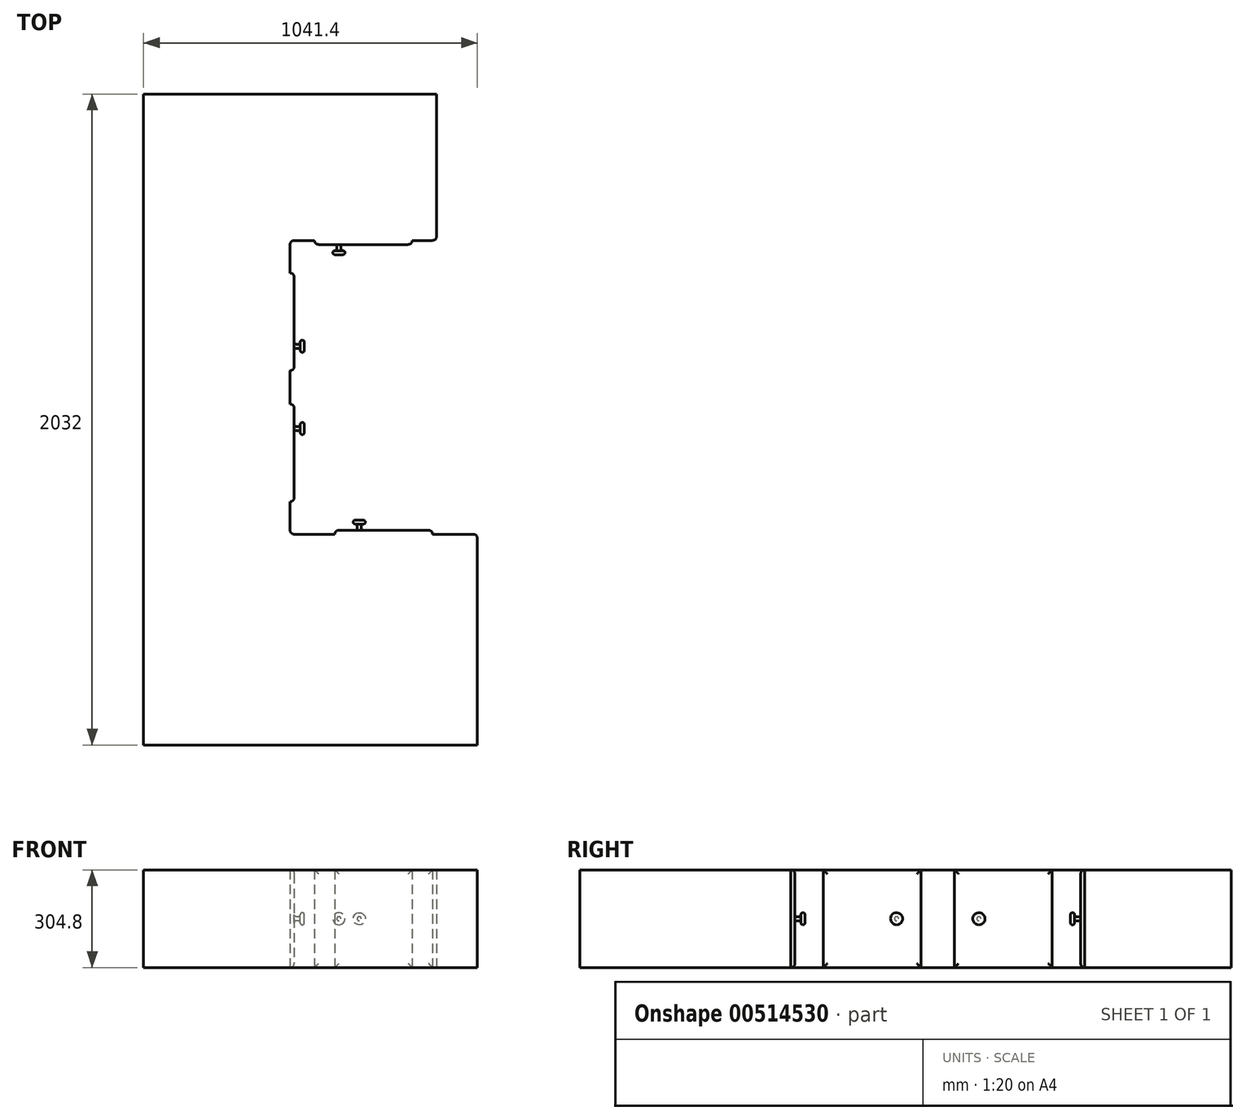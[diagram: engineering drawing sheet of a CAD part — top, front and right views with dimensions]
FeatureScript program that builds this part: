
annotation { "Feature Type Name" : "Feature", "Feature Type Description" : "" }
export const myFeature = defineFeature(function(context is Context, id is Id, definition is map)
    precondition{}
    {
        {
            var Q0;
            Q0=qCreatedBy(makeId("Top.planeOp"),FACE);
            var sketch = newSketch(context, id + "F0", { "sketchPlane" : qUnion([Q0])});
            skLineSegment(sketch, "E0.bottom", {"start": v(0, 0) * mm, "end": v(-914.4, 0) * mm});
            skLineSegment(sketch, "E0.top", {"start": v(0, 457.2) * mm, "end": v(-914.4, 457.2) * mm});
            skLineSegment(sketch, "E0.left", {"start": v(0, 0) * mm, "end": v(0, 457.2) * mm});
            skLineSegment(sketch, "E0.right", {"start": v(-914.4, 0) * mm, "end": v(-914.4, 457.2) * mm});
            skLineSegment(sketch, "E1", {"start": v(-914.4, 0) * mm, "end": v(-914.4, -1574.8) * mm});
            skLineSegment(sketch, "E2.bottom", {"start": v(-914.4, -1574.8) * mm, "end": v(127, -1574.8) * mm});
            skLineSegment(sketch, "E2.top", {"start": v(-914.4, -917.14) * mm, "end": v(127, -917.14) * mm});
            skLineSegment(sketch, "E2.left", {"start": v(-914.4, -1574.8) * mm, "end": v(-914.4, -917.14) * mm});
            skLineSegment(sketch, "E2.right", {"start": v(127, -1574.8) * mm, "end": v(127, -917.14) * mm});
            skLineSegment(sketch, "E3", {"start": v(-457.2, -917.14) * mm, "end": v(-457.2, 0) * mm});
            skSolve(sketch);
        }
        {
            var Q0;
            Q0=makeQuery(id+"F0.imprint","IMPRINT",FACE,{"disambiguationData":[TD([[makeQuery(id+"F0.imprint","IMPRINT",EDGE,{"derivedFrom":sQuery(id+"F0.wireOp",EDGE,"E0.top")}),1.0]])]});
            var Q1;
            {var subQ0=sQuery(id+"F0.wireOp",EDGE,"E3");Q1=makeQuery(id+"F0.imprint","IMPRINT",FACE,{"disambiguationData":[TD([[makeQuery(id+"F0.imprint","IMPRINT",EDGE,{"derivedFrom":subQ0}),1.0]])]});}
            var Q2;
            {var subQ5=sQuery(id+"F0.wireOp",EDGE,"E2.bottom");Q2=makeQuery(id+"F0.imprint","IMPRINT",FACE,{"disambiguationData":[TD([[makeQuery(id+"F0.imprint","IMPRINT",EDGE,{"derivedFrom":subQ5}),1.0]])]});}
            extrude(context, id + "F1", {"entities" : qUnion([Q0, Q1, Q2]), "depth" : 304.8 * mm, "offsetDistance" : 25.4 * mm});
        }
        {
            var Q0;
            Q0=makeQuery(id+"F1.opExtrude","SWEPT_EDGE",EDGE,{"disambiguationData":[OSD([sQuery(id+"F0.wireOp",EDGE,"E0.bottom"),sQuery(id+"F0.wireOp",EDGE,"E0.left")])]});
            var Q1;
            Q1=makeQuery(id+"F1.opExtrude","SWEPT_EDGE",EDGE,{"disambiguationData":[OSD([sQuery(id+"F0.wireOp",EDGE,"E0.bottom"),sQuery(id+"F0.wireOp",EDGE,"E3")])]});
            var Q2;
            Q2=makeQuery(id+"F1.opExtrude","SWEPT_EDGE",EDGE,{"disambiguationData":[OSD([sQuery(id+"F0.wireOp",EDGE,"E2.top"),sQuery(id+"F0.wireOp",EDGE,"E3")])]});
            var Q3;
            Q3=makeQuery(id+"F1.opExtrude","SWEPT_EDGE",EDGE,{"disambiguationData":[OSD([sQuery(id+"F0.wireOp",EDGE,"E2.top"),sQuery(id+"F0.wireOp",EDGE,"E2.right")])]});
            fillet(context, id + "F2", {"entities" : qUnion([Q0, Q1, Q2, Q3]), "radius" : 12.7 * mm, "tangentPropagation" : true, "allowEdgeOverflow" : false});
        }
        {
            var Q0;
            Q0=makeQuery(id+"F1.opExtrude","SWEPT_FACE",FACE,{"disambiguationData":[OSD([sQuery(id+"F0.wireOp",EDGE,"E2.top")])]});
            var sketch = newSketch(context, id + "F3", { "sketchPlane" : qUnion([Q0])});
            skLineSegment(sketch, "E4.bottom", {"start": v(12.7, 304.8) * mm, "end": v(317.5, 304.8) * mm});
            skLineSegment(sketch, "E4.top", {"start": v(12.7, 0) * mm, "end": v(317.5, 0) * mm});
            skLineSegment(sketch, "E4.left", {"start": v(12.7, 304.8) * mm, "end": v(12.7, 0) * mm});
            skLineSegment(sketch, "E4.right", {"start": v(317.5, 304.8) * mm, "end": v(317.5, 0) * mm});
            skSolve(sketch);
        }
        {
            var Q0;
            Q0=makeQuery(id+"F3.imprint","IMPRINT",FACE,{"disambiguationData":[TD([[makeQuery(id+"F3.imprint","IMPRINT",EDGE,{"derivedFrom":sQuery(id+"F3.wireOp",EDGE,"E4.bottom")}),1.0]])]});
            extrude(context, id + "F4", {"entities" : qUnion([Q0]), "operationType" : NewBodyOperationType.ADD, "depth" : 12.7 * mm, "offsetDistance" : 25.4 * mm});
        }
        {
            var Q0;
            Q0=makeQuery(id+"F1.opExtrude","SWEPT_FACE",FACE,{"disambiguationData":[OSD([sQuery(id+"F0.wireOp",EDGE,"E3")])]});
            var sketch = newSketch(context, id + "F5", { "sketchPlane" : qUnion([Q0])});
            skLineSegment(sketch, "E5.bottom", {"start": v(-815.54, 304.8) * mm, "end": v(-510.74, 304.8) * mm});
            skLineSegment(sketch, "E5.top", {"start": v(-815.54, 0) * mm, "end": v(-510.74, 0) * mm});
            skLineSegment(sketch, "E5.left", {"start": v(-815.54, 304.8) * mm, "end": v(-815.54, 0) * mm});
            skLineSegment(sketch, "E5.right", {"start": v(-510.74, 304.8) * mm, "end": v(-510.74, 0) * mm});
            skLineSegment(sketch, "E6.bottom", {"start": v(-406.4, 304.8) * mm, "end": v(-101.6, 304.8) * mm});
            skLineSegment(sketch, "E6.top", {"start": v(-406.4, 0) * mm, "end": v(-101.6, 0) * mm});
            skLineSegment(sketch, "E6.left", {"start": v(-406.4, 304.8) * mm, "end": v(-406.4, 0) * mm});
            skLineSegment(sketch, "E6.right", {"start": v(-101.6, 304.8) * mm, "end": v(-101.6, 0) * mm});
            skSolve(sketch);
        }
        {
            var Q0;
            Q0=makeQuery(id+"F5.imprint","IMPRINT",FACE,{"disambiguationData":[TD([[makeQuery(id+"F5.imprint","IMPRINT",EDGE,{"derivedFrom":sQuery(id+"F5.wireOp",EDGE,"E5.bottom")}),-1.0]])]});
            var Q1;
            Q1=makeQuery(id+"F5.imprint","IMPRINT",FACE,{"disambiguationData":[TD([[makeQuery(id+"F5.imprint","IMPRINT",EDGE,{"derivedFrom":sQuery(id+"F5.wireOp",EDGE,"E6.bottom")}),-1.0]])]});
            extrude(context, id + "F6", {"entities" : qUnion([Q0, Q1]), "operationType" : NewBodyOperationType.ADD, "depth" : 12.7 * mm, "offsetDistance" : 25.4 * mm});
        }
        {
            var Q0;
            Q0=makeQuery(id+"F1.opExtrude","SWEPT_FACE",FACE,{"disambiguationData":[OSD([sQuery(id+"F0.wireOp",EDGE,"E0.bottom")])]});
            var sketch = newSketch(context, id + "F7", { "sketchPlane" : qUnion([Q0])});
            skLineSegment(sketch, "E7.bottom", {"start": v(-381, 304.8) * mm, "end": v(-76.2, 304.8) * mm});
            skLineSegment(sketch, "E7.top", {"start": v(-381, 0) * mm, "end": v(-76.2, 0) * mm});
            skLineSegment(sketch, "E7.left", {"start": v(-381, 304.8) * mm, "end": v(-381, 0) * mm});
            skLineSegment(sketch, "E7.right", {"start": v(-76.2, 304.8) * mm, "end": v(-76.2, 0) * mm});
            skSolve(sketch);
        }
        {
            var Q0;
            Q0=makeQuery(id+"F7.imprint","IMPRINT",FACE,{"disambiguationData":[TD([[makeQuery(id+"F7.imprint","IMPRINT",EDGE,{"derivedFrom":sQuery(id+"F7.wireOp",EDGE,"E7.bottom")}),1.0]])]});
            extrude(context, id + "F8", {"entities" : qUnion([Q0]), "operationType" : NewBodyOperationType.ADD, "depth" : 12.7 * mm, "offsetDistance" : 25.4 * mm});
        }
        {
            var Q0;
            Q0=makeQuery(id+"F4.opExtrude","CAP_EDGE",EDGE,{"disambiguationData":[OSD([sQuery(id+"F3.wireOp",EDGE,"E4.left")])],"isStart":false});
            var Q1;
            Q1=makeQuery(id+"F4.opExtrude","CAP_EDGE",EDGE,{"disambiguationData":[OSD([sQuery(id+"F3.wireOp",EDGE,"E4.bottom")])],"isStart":false});
            var Q2;
            Q2=makeQuery(id+"F4.opExtrude","CAP_EDGE",EDGE,{"disambiguationData":[OSD([sQuery(id+"F3.wireOp",EDGE,"E4.right")])],"isStart":false});
            var Q3;
            Q3=makeQuery(id+"F4.opExtrude","CAP_EDGE",EDGE,{"disambiguationData":[OSD([sQuery(id+"F3.wireOp",EDGE,"E4.top")])],"isStart":false});
            var Q4;
            Q4=makeQuery(id+"F6.opExtrude","CAP_EDGE",EDGE,{"disambiguationData":[OSD([sQuery(id+"F5.wireOp",EDGE,"E5.left")])],"isStart":false});
            var Q5;
            Q5=makeQuery(id+"F6.opExtrude","CAP_EDGE",EDGE,{"disambiguationData":[OSD([sQuery(id+"F5.wireOp",EDGE,"E5.bottom")])],"isStart":false});
            var Q6;
            Q6=makeQuery(id+"F6.opExtrude","CAP_EDGE",EDGE,{"disambiguationData":[OSD([sQuery(id+"F5.wireOp",EDGE,"E5.right")])],"isStart":false});
            var Q7;
            Q7=makeQuery(id+"F6.opExtrude","CAP_EDGE",EDGE,{"disambiguationData":[OSD([sQuery(id+"F5.wireOp",EDGE,"E5.top")])],"isStart":false});
            var Q8;
            Q8=makeQuery(id+"F6.opExtrude","CAP_EDGE",EDGE,{"disambiguationData":[OSD([sQuery(id+"F5.wireOp",EDGE,"E6.left")])],"isStart":false});
            var Q9;
            Q9=makeQuery(id+"F6.opExtrude","CAP_EDGE",EDGE,{"disambiguationData":[OSD([sQuery(id+"F5.wireOp",EDGE,"E6.bottom")])],"isStart":false});
            var Q10;
            Q10=makeQuery(id+"F6.opExtrude","CAP_EDGE",EDGE,{"disambiguationData":[OSD([sQuery(id+"F5.wireOp",EDGE,"E6.top")])],"isStart":false});
            var Q11;
            Q11=makeQuery(id+"F6.opExtrude","CAP_FACE",FACE,{"disambiguationData":[OSD([sQuery(id+"F5.wireOp",EDGE,"E6.bottom"),sQuery(id+"F5.wireOp",EDGE,"E6.top"),sQuery(id+"F5.wireOp",EDGE,"E6.left"),sQuery(id+"F5.wireOp",EDGE,"E6.right")])],"isStart":false});
            var Q12;
            Q12=makeQuery(id+"F8.opExtrude","CAP_FACE",FACE,{"disambiguationData":[OSD([sQuery(id+"F7.wireOp",EDGE,"E7.bottom"),sQuery(id+"F7.wireOp",EDGE,"E7.top"),sQuery(id+"F7.wireOp",EDGE,"E7.left"),sQuery(id+"F7.wireOp",EDGE,"E7.right")])],"isStart":false});
            fillet(context, id + "F9", {"entities" : qUnion([Q0, Q1, Q2, Q3, Q4, Q5, Q6, Q7, Q8, Q9, Q10, Q11, Q12]), "radius" : 12.7 * mm, "tangentPropagation" : true, "allowEdgeOverflow" : false});
        }
        {
            var Q0;
            Q0=makeQuery(id+"F4.opExtrude","CAP_FACE",FACE,{"disambiguationData":[OSD([sQuery(id+"F3.wireOp",EDGE,"E4.bottom"),sQuery(id+"F3.wireOp",EDGE,"E4.top"),sQuery(id+"F3.wireOp",EDGE,"E4.left"),sQuery(id+"F3.wireOp",EDGE,"E4.right")])],"isStart":false});
            var sketch = newSketch(context, id + "F10", { "sketchPlane" : qUnion([Q0])});
            skCircle(sketch, "E8", {"center": v(241.3, 152.4) * mm, "radius": 6.35 * mm});
            skLineSegment(sketch, "E9", {"start": v(241.3, 152.4) * mm, "end": v(304.8, 152.4) * mm});
            skSolve(sketch);
        }
        {
            var Q0;
            Q0=makeQuery(id+"F10.imprint","IMPRINT",FACE,{"disambiguationData":[TD([[makeQuery(id+"F10.imprint","IMPRINT",EDGE,{"derivedFrom":sQuery(id+"F10.wireOp",EDGE,"E8")}),1.0]])]});
            extrude(context, id + "F11", {"entities" : qUnion([Q0]), "operationType" : NewBodyOperationType.ADD, "depth" : 19.05 * mm, "offsetDistance" : 25.4 * mm});
        }
        {
            var Q0;
            Q0=makeQuery(id+"F11.opExtrude","CAP_FACE",FACE,{"disambiguationData":[OSD([sQuery(id+"F10.wireOp",EDGE,"E8")])],"isStart":false});
            var sketch = newSketch(context, id + "F12", { "sketchPlane" : qUnion([Q0])});
            skCircle(sketch, "E10", {"center": v(241.3, 152.4) * mm, "radius": 19.05 * mm});
            skSolve(sketch);
        }
        {
            var Q0;
            Q0=makeQuery(id+"F12.imprint","IMPRINT",FACE,{"disambiguationData":[TD([[makeQuery(id+"F12.imprint","IMPRINT",EDGE,{"derivedFrom":makeQuery(id+"F11.opExtrude","CAP_EDGE",EDGE,{"disambiguationData":[OSD([sQuery(id+"F10.wireOp",EDGE,"E8")])],"isStart":false})}),1.0]])]});
            var Q1;
            Q1=makeQuery(id+"F12.imprint","IMPRINT",FACE,{"disambiguationData":[TD([[makeQuery(id+"F12.imprint","IMPRINT",EDGE,{"derivedFrom":sQuery(id+"F12.wireOp",EDGE,"E10")}),1.0]])]});
            extrude(context, id + "F13", {"entities" : qUnion([Q0, Q1]), "operationType" : NewBodyOperationType.ADD, "depth" : 12.7 * mm, "offsetDistance" : 25.4 * mm});
        }
        {
            var Q0;
            Q0=makeQuery(id+"F13.opExtrude","SWEPT_FACE",FACE,{"disambiguationData":[OSD([sQuery(id+"F12.wireOp",EDGE,"E10")])]});
            var Q1;
            Q1=makeQuery(id+"F13.opExtrude","CAP_FACE",FACE,{"disambiguationData":[OSD([sQuery(id+"F12.wireOp",EDGE,"E10")])],"isStart":false});
            var Q2;
            Q2=makeQuery(id+"F11.opExtrude","SWEPT_FACE",FACE,{"disambiguationData":[OSD([sQuery(id+"F10.wireOp",EDGE,"E8")])]});
            fillet(context, id + "F14", {"entities" : qUnion([Q0, Q1, Q2]), "radius" : 6.35 * mm, "tangentPropagation" : true, "allowEdgeOverflow" : false});
        }
        {
            var Q0;
            Q0=makeQuery(id+"F6.opExtrude","CAP_FACE",FACE,{"disambiguationData":[OSD([sQuery(id+"F5.wireOp",EDGE,"E5.bottom"),sQuery(id+"F5.wireOp",EDGE,"E5.top"),sQuery(id+"F5.wireOp",EDGE,"E5.left"),sQuery(id+"F5.wireOp",EDGE,"E5.right")])],"isStart":false});
            var sketch = newSketch(context, id + "F15", { "sketchPlane" : qUnion([Q0])});
            skCircle(sketch, "E11", {"center": v(-586.94, 152.4) * mm, "radius": 6.35 * mm});
            skCircle(sketch, "E12", {"center": v(-330.2, 152.4) * mm, "radius": 6.35 * mm});
            skLineSegment(sketch, "E13", {"start": v(-586.94, 152.4) * mm, "end": v(-802.84, 152.4) * mm});
            skLineSegment(sketch, "E14", {"start": v(-586.94, 152.4) * mm, "end": v(-586.94, 292.1) * mm});
            skLineSegment(sketch, "E15", {"start": v(-330.2, 152.4) * mm, "end": v(-114.3, 152.4) * mm});
            skLineSegment(sketch, "E16", {"start": v(-330.2, 152.4) * mm, "end": v(-330.2, 292.1) * mm});
            skSolve(sketch);
        }
        {
            var Q0;
            {var subQ0=sQuery(id+"F15.wireOp",EDGE,"E13");var subQ1=sQuery(id+"F15.wireOp",EDGE,"E11");var subQ2=makeQuery(id+"F15.imprint","INTERSECT",VERTEX,{"derivedFrom":[subQ1,subQ0]});Q0=makeQuery(id+"F15.imprint","IMPRINT",FACE,{"disambiguationData":[TD([[makeQuery(id+"F15.imprint","IMPRINT",EDGE,{"disambiguationData":[TD([[subQ2,1.0]])],"derivedFrom":subQ1}),1.0]])]});}
            var Q1;
            {var subQ0=sQuery(id+"F15.wireOp",EDGE,"E13");var subQ1=sQuery(id+"F15.wireOp",EDGE,"E11");var subQ2=makeQuery(id+"F15.imprint","INTERSECT",VERTEX,{"derivedFrom":[subQ1,subQ0]});Q1=makeQuery(id+"F15.imprint","IMPRINT",FACE,{"disambiguationData":[TD([[makeQuery(id+"F15.imprint","IMPRINT",EDGE,{"disambiguationData":[TD([[subQ2,-1.0]])],"derivedFrom":subQ1}),1.0]])]});}
            var Q2;
            {var subQ0=sQuery(id+"F15.wireOp",EDGE,"E15");var subQ1=sQuery(id+"F15.wireOp",EDGE,"E12");var subQ2=makeQuery(id+"F15.imprint","INTERSECT",VERTEX,{"derivedFrom":[subQ1,subQ0]});Q2=makeQuery(id+"F15.imprint","IMPRINT",FACE,{"disambiguationData":[TD([[makeQuery(id+"F15.imprint","IMPRINT",EDGE,{"disambiguationData":[TD([[subQ2,-1.0]])],"derivedFrom":subQ1}),1.0]])]});}
            var Q3;
            {var subQ0=sQuery(id+"F15.wireOp",EDGE,"E15");var subQ1=sQuery(id+"F15.wireOp",EDGE,"E12");var subQ2=makeQuery(id+"F15.imprint","INTERSECT",VERTEX,{"derivedFrom":[subQ1,subQ0]});Q3=makeQuery(id+"F15.imprint","IMPRINT",FACE,{"disambiguationData":[TD([[makeQuery(id+"F15.imprint","IMPRINT",EDGE,{"disambiguationData":[TD([[subQ2,1.0]])],"derivedFrom":subQ1}),1.0]])]});}
            extrude(context, id + "F16", {"entities" : qUnion([Q0, Q1, Q2, Q3]), "operationType" : NewBodyOperationType.ADD, "depth" : 19.05 * mm, "offsetDistance" : 25.4 * mm});
        }
        {
            var Q0;
            Q0=makeQuery(id+"F16.opExtrude","CAP_FACE",FACE,{"disambiguationData":[OSD([sQuery(id+"F15.wireOp",EDGE,"E11")])],"isStart":false});
            var sketch = newSketch(context, id + "F17", { "sketchPlane" : qUnion([Q0])});
            skCircle(sketch, "E17", {"center": v(-586.94, 152.4) * mm, "radius": 19.05 * mm});
            skCircle(sketch, "E18", {"center": v(-330.2, 152.4) * mm, "radius": 19.05 * mm});
            skSolve(sketch);
        }
        {
            var Q0;
            Q0=makeQuery(id+"F17.imprint","IMPRINT",FACE,{"disambiguationData":[TD([[makeQuery(id+"F17.imprint","IMPRINT",EDGE,{"derivedFrom":makeQuery(id+"F16.opExtrude","CAP_EDGE",EDGE,{"disambiguationData":[OSD([sQuery(id+"F15.wireOp",EDGE,"E11")])],"isStart":false})}),1.0]])]});
            var Q1;
            Q1=makeQuery(id+"F17.imprint","IMPRINT",FACE,{"disambiguationData":[TD([[makeQuery(id+"F17.imprint","IMPRINT",EDGE,{"derivedFrom":sQuery(id+"F17.wireOp",EDGE,"E17")}),1.0]])]});
            var Q2;
            Q2=makeQuery(id+"F17.imprint","IMPRINT",FACE,{"disambiguationData":[TD([[makeQuery(id+"F17.imprint","IMPRINT",EDGE,{"derivedFrom":sQuery(id+"F17.wireOp",EDGE,"E18")}),1.0]])]});
            extrude(context, id + "F18", {"entities" : qUnion([Q0, Q1, Q2]), "operationType" : NewBodyOperationType.ADD, "depth" : 12.7 * mm, "offsetDistance" : 25.4 * mm});
        }
        {
            var Q0;
            Q0=makeQuery(id+"F18.opExtrude","SWEPT_FACE",FACE,{"disambiguationData":[OSD([sQuery(id+"F17.wireOp",EDGE,"E17")])]});
            var Q1;
            Q1=makeQuery(id+"F16.opExtrude","SWEPT_FACE",FACE,{"disambiguationData":[OSD([sQuery(id+"F15.wireOp",EDGE,"E11")])]});
            var Q2;
            Q2=makeQuery(id+"F16.opExtrude","SWEPT_FACE",FACE,{"disambiguationData":[OSD([sQuery(id+"F15.wireOp",EDGE,"E12")])]});
            var Q3;
            Q3=makeQuery(id+"F18.opExtrude","SWEPT_FACE",FACE,{"disambiguationData":[OSD([sQuery(id+"F17.wireOp",EDGE,"E18")])]});
            fillet(context, id + "F19", {"entities" : qUnion([Q0, Q1, Q2, Q3]), "radius" : 6.35 * mm, "tangentPropagation" : true, "allowEdgeOverflow" : false});
        }
        {
            var Q0;
            Q0=makeQuery(id+"F8.opExtrude","CAP_FACE",FACE,{"disambiguationData":[OSD([sQuery(id+"F7.wireOp",EDGE,"E7.bottom"),sQuery(id+"F7.wireOp",EDGE,"E7.top"),sQuery(id+"F7.wireOp",EDGE,"E7.left"),sQuery(id+"F7.wireOp",EDGE,"E7.right")])],"isStart":false});
            var sketch = newSketch(context, id + "F20", { "sketchPlane" : qUnion([Q0])});
            skCircle(sketch, "E19", {"center": v(-304.8, 152.4) * mm, "radius": 6.35 * mm});
            skLineSegment(sketch, "E20", {"start": v(-304.8, 152.4) * mm, "end": v(-304.8, 292.1) * mm});
            skLineSegment(sketch, "E21", {"start": v(-304.8, 152.4) * mm, "end": v(-368.3, 152.4) * mm});
            skSolve(sketch);
        }
        {
            var Q0;
            {var subQ0=sQuery(id+"F20.wireOp",EDGE,"E20");var subQ1=sQuery(id+"F20.wireOp",EDGE,"E19");var subQ2=makeQuery(id+"F20.imprint","INTERSECT",VERTEX,{"derivedFrom":[subQ1,subQ0]});Q0=makeQuery(id+"F20.imprint","IMPRINT",FACE,{"disambiguationData":[TD([[makeQuery(id+"F20.imprint","IMPRINT",EDGE,{"disambiguationData":[TD([[subQ2,-1.0]])],"derivedFrom":subQ1}),1.0]])]});}
            var Q1;
            {var subQ0=sQuery(id+"F20.wireOp",EDGE,"E20");var subQ1=sQuery(id+"F20.wireOp",EDGE,"E19");var subQ2=makeQuery(id+"F20.imprint","INTERSECT",VERTEX,{"derivedFrom":[subQ1,subQ0]});Q1=makeQuery(id+"F20.imprint","IMPRINT",FACE,{"disambiguationData":[TD([[makeQuery(id+"F20.imprint","IMPRINT",EDGE,{"disambiguationData":[TD([[subQ2,1.0]])],"derivedFrom":subQ1}),1.0]])]});}
            extrude(context, id + "F21", {"entities" : qUnion([Q0, Q1]), "operationType" : NewBodyOperationType.ADD, "depth" : 19.05 * mm, "offsetDistance" : 25.4 * mm});
        }
        {
            var Q0;
            Q0=makeQuery(id+"F21.opExtrude","CAP_FACE",FACE,{"disambiguationData":[OSD([sQuery(id+"F20.wireOp",EDGE,"E19")])],"isStart":false});
            var sketch = newSketch(context, id + "F22", { "sketchPlane" : qUnion([Q0])});
            skCircle(sketch, "E22", {"center": v(-304.8, 152.4) * mm, "radius": 19.05 * mm});
            skSolve(sketch);
        }
        {
            var Q0;
            Q0=makeQuery(id+"F22.imprint","IMPRINT",FACE,{"disambiguationData":[TD([[makeQuery(id+"F22.imprint","IMPRINT",EDGE,{"derivedFrom":makeQuery(id+"F21.opExtrude","CAP_EDGE",EDGE,{"disambiguationData":[OSD([sQuery(id+"F20.wireOp",EDGE,"E19")])],"isStart":false})}),1.0]])]});
            var Q1;
            Q1=makeQuery(id+"F22.imprint","IMPRINT",FACE,{"disambiguationData":[TD([[makeQuery(id+"F22.imprint","IMPRINT",EDGE,{"derivedFrom":sQuery(id+"F22.wireOp",EDGE,"E22")}),1.0]])]});
            extrude(context, id + "F23", {"entities" : qUnion([Q0, Q1]), "operationType" : NewBodyOperationType.ADD, "depth" : 12.7 * mm, "offsetDistance" : 25.4 * mm});
        }
        {
            var Q0;
            Q0=makeQuery(id+"F23.opExtrude","SWEPT_FACE",FACE,{"disambiguationData":[OSD([sQuery(id+"F22.wireOp",EDGE,"E22")])]});
            var Q1;
            Q1=makeQuery(id+"F21.opExtrude","SWEPT_FACE",FACE,{"disambiguationData":[OSD([sQuery(id+"F20.wireOp",EDGE,"E19")])]});
            fillet(context, id + "F24", {"entities" : qUnion([Q0, Q1]), "radius" : 6.35 * mm, "tangentPropagation" : true, "allowEdgeOverflow" : false});
        }
    });
